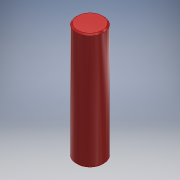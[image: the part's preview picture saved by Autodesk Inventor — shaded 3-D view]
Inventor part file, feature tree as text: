
AUTODESK INVENTOR PART (.ipt)
format: ipt  version: 2018 (Build 220112000, 112)  size: 102,400 bytes
history: native  units: mm
features: extrude x1, chamfer x1, sketch x1
ambient origin geometry x8: Origin, YZ Plane, XZ Plane, XY Plane, X Axis, Y Axis, Z Axis, Center Point
bodies: Solido1 (feature_tree)
feature tree (3):
  extrude  "Estrusione1"  Depth=10.0mm
  chamfer  "Smusso1"  Distance=42.0mm
  sketch  "Schizzo1"
